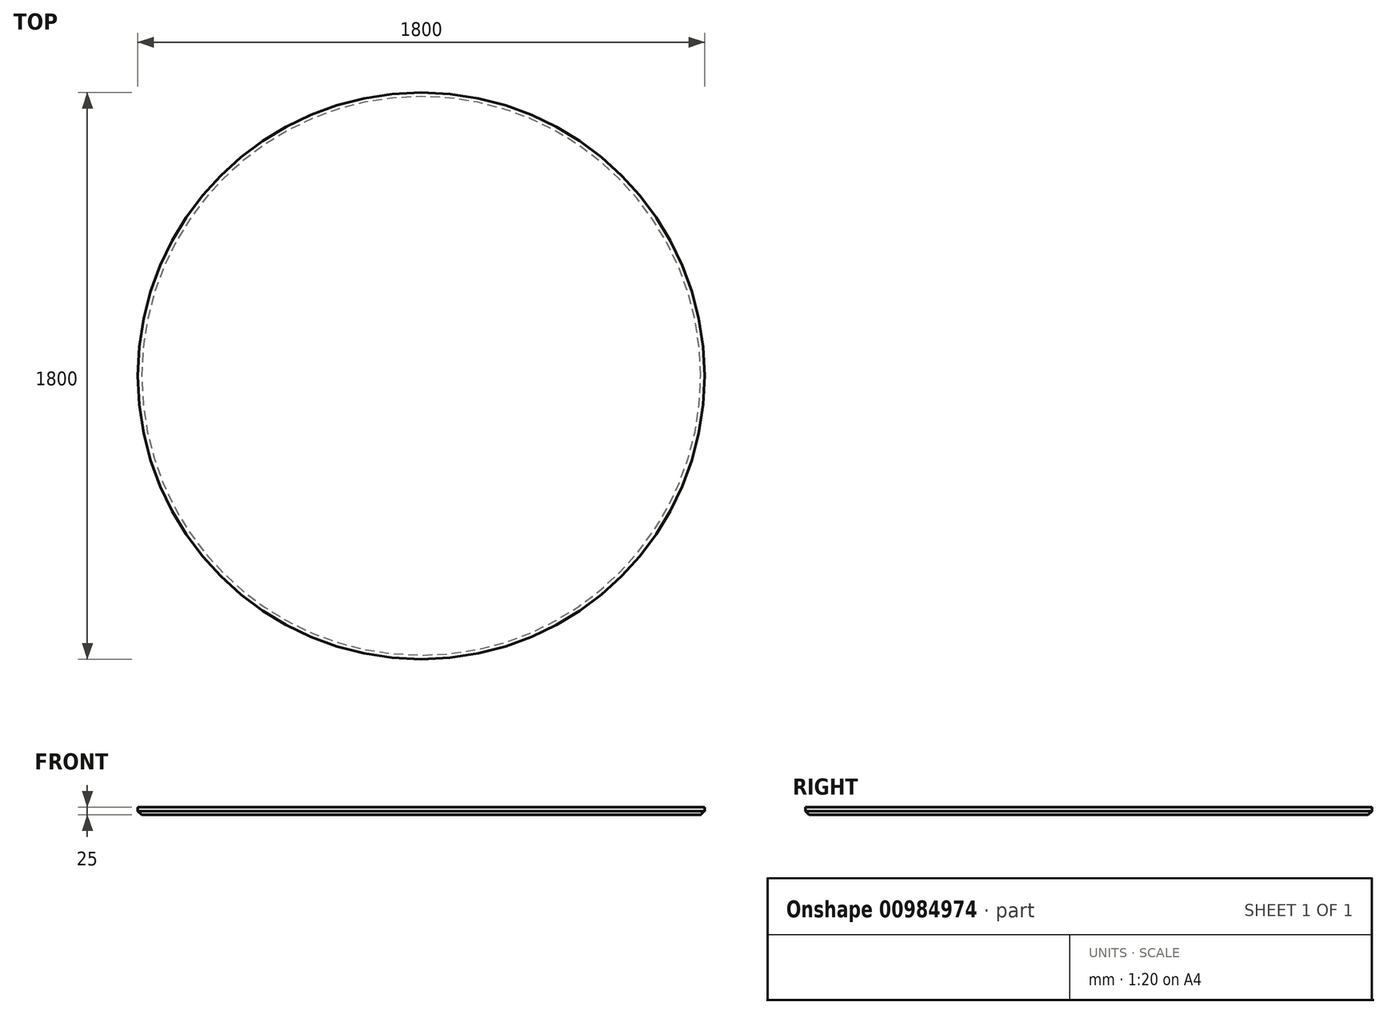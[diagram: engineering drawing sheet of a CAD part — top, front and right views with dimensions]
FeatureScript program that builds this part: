
annotation { "Feature Type Name" : "Feature", "Feature Type Description" : "" }
export const myFeature = defineFeature(function(context is Context, id is Id, definition is map)
    precondition{}
    {
        {
            var Q0;
            Q0=qCreatedBy(makeId("Top.planeOp"),FACE);
            var sketch = newSketch(context, id + "F0", { "sketchPlane" : qUnion([Q0])});
            skCircle(sketch, "E0", {"center": v(0, 0) * mm, "radius": 900 * mm});
            skSolve(sketch);
        }
        {
            var Q0;
            Q0 = qSketchRegion(id + "F0", true);
            extrude(context, id + "F1", {"entities" : qUnion([Q0]), "depth" : 25 * mm, "offsetDistance" : 25 * mm});
        }
        {
            var Q0;
            Q0=makeQuery(id+"F1.opExtrude","CAP_EDGE",EDGE,{"disambiguationData":[OSD([sQuery(id+"F0.wireOp",EDGE,"E0")])],"isStart":true});
            chamfer(context, id + "F2", {"entities" : qUnion([Q0]), "chamferType" : ChamferType.TWO_OFFSETS, "width1" : 12.5 * mm, "oppositeDirection" : false, "width2" : 12.5 * mm, "tangentPropagation" : true});
        }
        {
            var Q0;
            Q0=makeQuery(id+"F1.opExtrude","CAP_EDGE",EDGE,{"disambiguationData":[OSD([sQuery(id+"F0.wireOp",EDGE,"E0")])],"isStart":false});
            fillet(context, id + "F3", {"entities" : qUnion([Q0]), "radius" : 3 * mm, "tangentPropagation" : true, "allowEdgeOverflow" : false});
        }
    });
